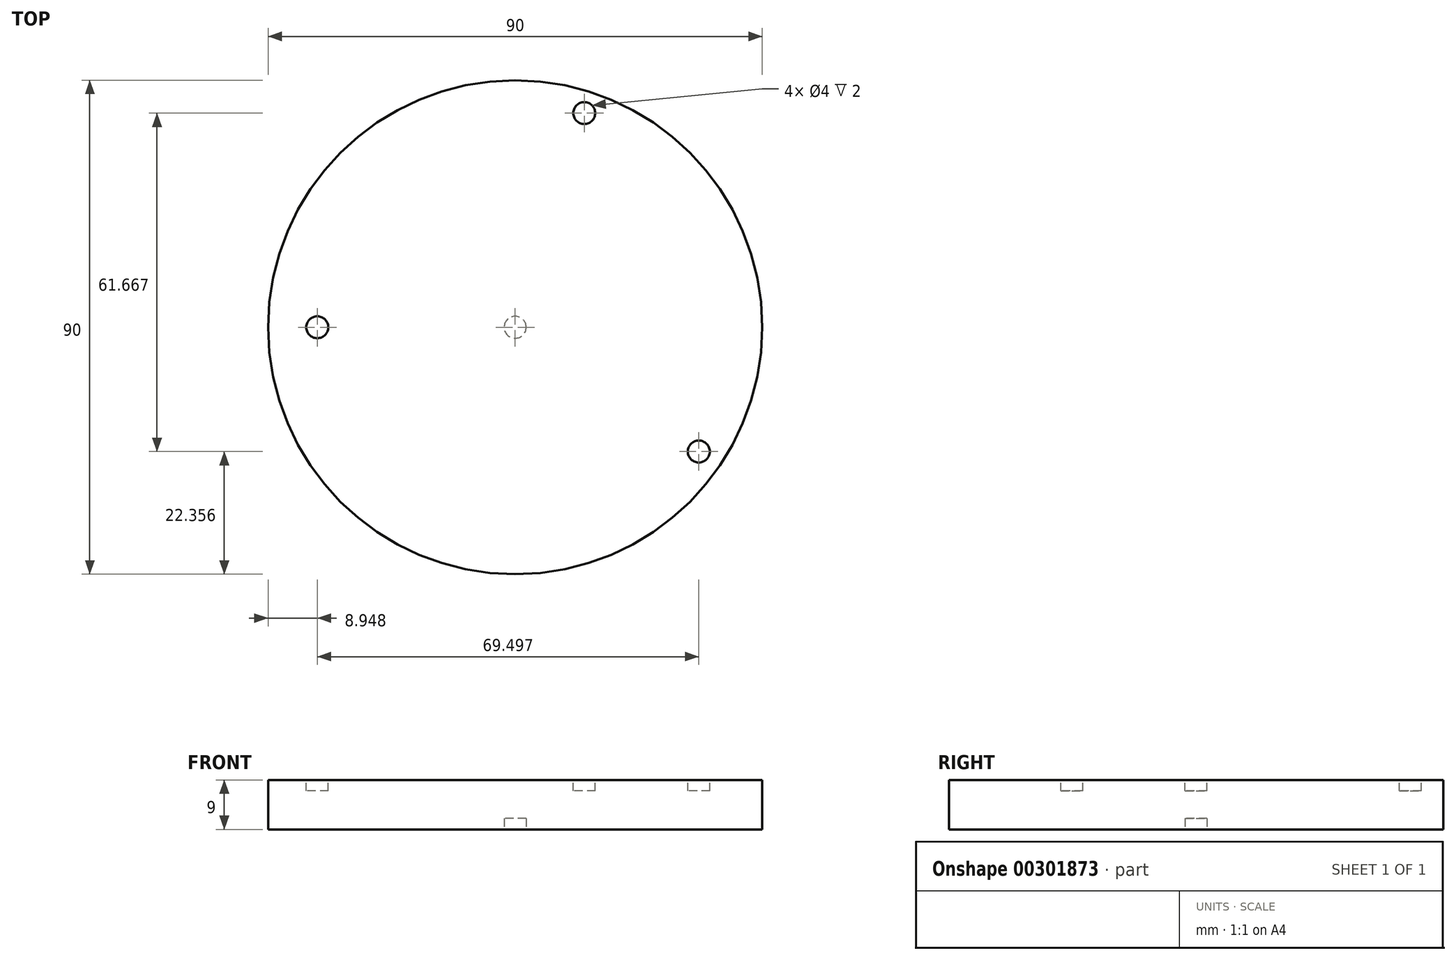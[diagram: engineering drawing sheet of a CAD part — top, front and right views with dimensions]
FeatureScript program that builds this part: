
annotation { "Feature Type Name" : "Feature", "Feature Type Description" : "" }
export const myFeature = defineFeature(function(context is Context, id is Id, definition is map)
    precondition{}
    {
        {
            var Q0;
            Q0=qCreatedBy(makeId("Top.planeOp"),FACE);
            var sketch = newSketch(context, id + "F0", { "sketchPlane" : qUnion([Q0])});
            skCircle(sketch, "E0", {"center": v(0, 0) * mm, "radius": 45 * mm});
            skCircle(sketch, "E1", {"center": v(0, 0) * mm, "radius": 2 * mm});
            skSolve(sketch);
        }
        {
            var Q0;
            Q0=makeQuery(id+"F0.imprint","IMPRINT",FACE,{"disambiguationData":[TD([[makeQuery(id+"F0.imprint","IMPRINT",EDGE,{"derivedFrom":sQuery(id+"F0.wireOp",EDGE,"E0")}),1.0]])]});
            var Q1;
            Q1=makeQuery(id+"F0.imprint","IMPRINT",FACE,{"disambiguationData":[TD([[makeQuery(id+"F0.imprint","IMPRINT",EDGE,{"derivedFrom":sQuery(id+"F0.wireOp",EDGE,"E1")}),1.0]])]});
            extrude(context, id + "F1", {"entities" : qUnion([Q0, Q1]), "depth" : 9 * mm});
        }
        {
            var Q0;
            Q0=makeQuery(id+"F0.imprint","IMPRINT",FACE,{"disambiguationData":[TD([[makeQuery(id+"F0.imprint","IMPRINT",EDGE,{"derivedFrom":sQuery(id+"F0.wireOp",EDGE,"E1")}),1.0]])]});
            extrude(context, id + "F2", {"entities" : qUnion([Q0]), "operationType" : NewBodyOperationType.REMOVE, "depth" : 2 * mm});
        }
        {
            var Q0;
            Q0=makeQuery(id+"F1.opExtrude","CAP_FACE",FACE,{"disambiguationData":[OSD([sQuery(id+"F0.wireOp",EDGE,"E0")])],"isStart":false});
            var sketch = newSketch(context, id + "F3", { "sketchPlane" : qUnion([Q0])});
            skCircle(sketch, "E2", {"center": v(12.58, 39.02) * mm, "radius": 2 * mm});
            skCircle(sketch, "E3", {"center": v(33.45, -22.64) * mm, "radius": 2 * mm});
            skCircle(sketch, "E4", {"center": v(-36.05, 0) * mm, "radius": 2 * mm});
            skCircle(sketch, "E5", {"center": v(4.45, 6.35) * mm, "radius": 45 * mm});
            skSolve(sketch);
        }
        {
            var Q0;
            Q0=makeQuery(id+"F3.imprint","IMPRINT",FACE,{"disambiguationData":[TD([[makeQuery(id+"F3.imprint","IMPRINT",EDGE,{"derivedFrom":sQuery(id+"F3.wireOp",EDGE,"E4")}),1.0]])]});
            var Q1;
            Q1=makeQuery(id+"F3.imprint","IMPRINT",FACE,{"disambiguationData":[TD([[makeQuery(id+"F3.imprint","IMPRINT",EDGE,{"derivedFrom":sQuery(id+"F3.wireOp",EDGE,"E2")}),1.0]])]});
            var Q2;
            Q2=makeQuery(id+"F3.imprint","IMPRINT",FACE,{"disambiguationData":[TD([[makeQuery(id+"F3.imprint","IMPRINT",EDGE,{"derivedFrom":sQuery(id+"F3.wireOp",EDGE,"E3")}),1.0]])]});
            extrude(context, id + "F4", {"entities" : qUnion([Q0, Q1, Q2]), "operationType" : NewBodyOperationType.REMOVE, "oppositeDirection" : true, "depth" : 2 * mm});
        }
    });
